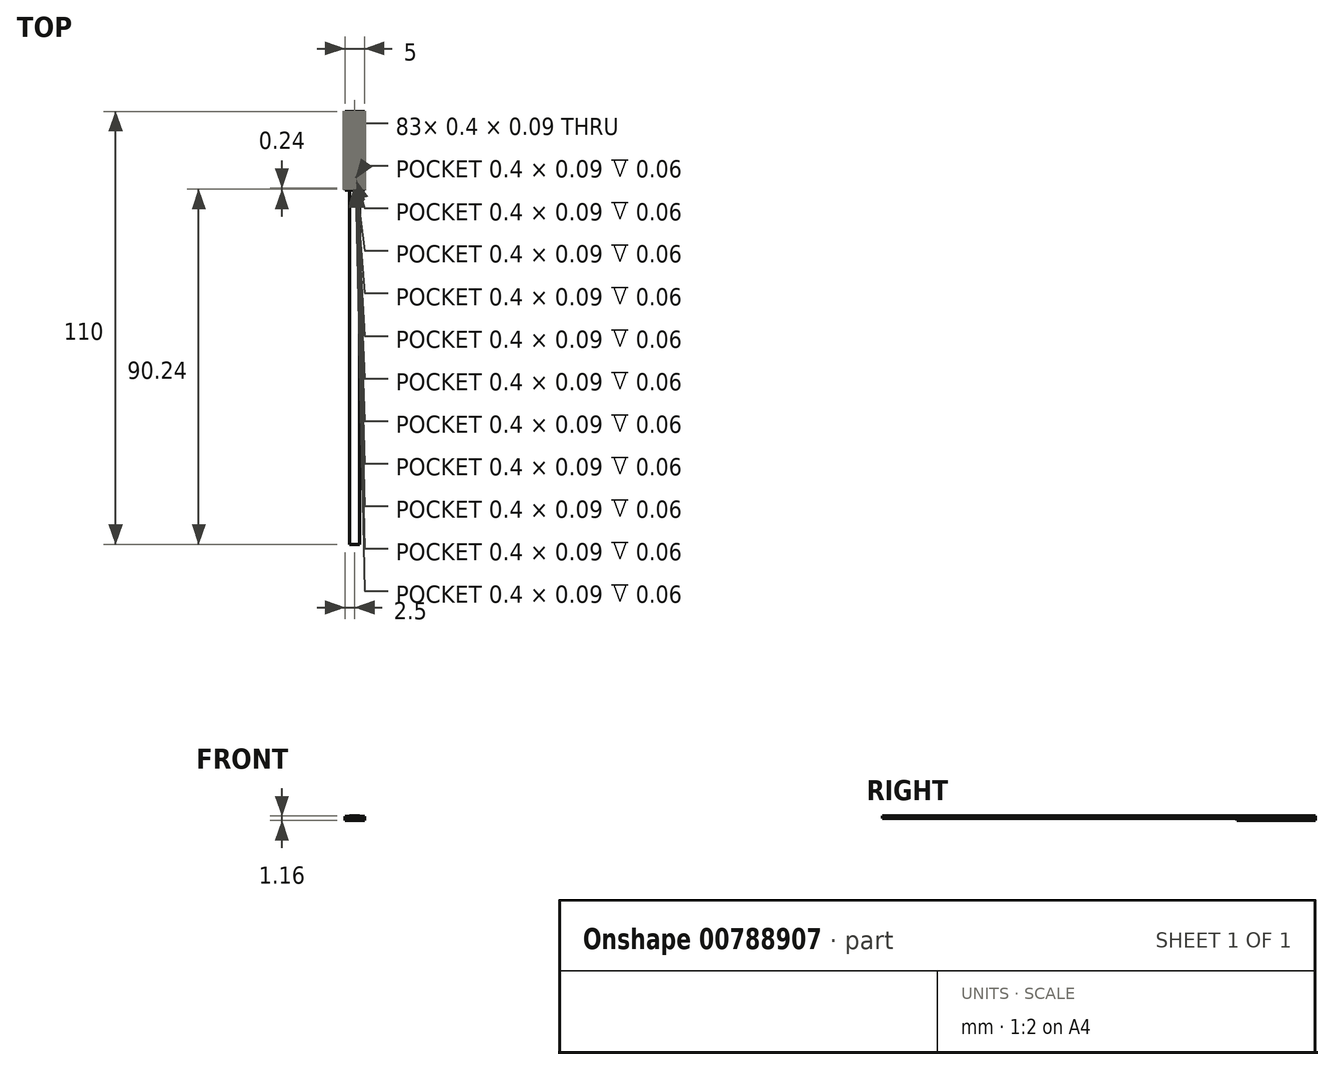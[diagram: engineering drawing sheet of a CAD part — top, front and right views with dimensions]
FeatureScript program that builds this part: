
annotation { "Feature Type Name" : "Feature", "Feature Type Description" : "" }
export const myFeature = defineFeature(function(context is Context, id is Id, definition is map)
    precondition{}
    {
        {
            assignVariable(context, id + "F0", {"name" : "Lz", "anyValue" : 20 * mm});
        }
        {
            var Q0;
            Q0=qCreatedBy(makeId("Top.planeOp"),FACE);
            var sketch = newSketch(context, id + "F1", { "sketchPlane" : qUnion([Q0])});
            skLineSegment(sketch, "E0.bottom", {"start": v(1.25, 10) * mm, "end": v(-1.25, 10) * mm});
            skLineSegment(sketch, "E0.top", {"start": v(1.25, -10) * mm, "end": v(-1.25, -10) * mm});
            skLineSegment(sketch, "E0.left", {"start": v(1.25, 10) * mm, "end": v(1.25, -10) * mm});
            skLineSegment(sketch, "E0.right", {"start": v(-1.25, 10) * mm, "end": v(-1.25, -10) * mm});
            skPoint(sketch, "E0.middle", {"position": v(0, 0) * mm});
            skLineSegment(sketch, "E1.bottom", {"start": v(2.5, 10) * mm, "end": v(-2.5, 10) * mm});
            skLineSegment(sketch, "E1.top", {"start": v(2.5, -10) * mm, "end": v(-2.5, -10) * mm});
            skLineSegment(sketch, "E1.left", {"start": v(2.5, 10) * mm, "end": v(2.5, -10) * mm});
            skLineSegment(sketch, "E1.right", {"start": v(-2.5, 10) * mm, "end": v(-2.5, -10) * mm});
            skSolve(sketch);
        }
        {
            var Q0;
            Q0=qCreatedBy(makeId("Front.planeOp"),FACE);
            var sketch = newSketch(context, id + "F2", { "sketchPlane" : qUnion([Q0])});
            skPoint(sketch, "E2", {"position": v(0.06, -0.1) * mm});
            skEllipse(sketch, "E3", {"center": v(0, -0.17) * mm, "majorRadius": 1.28 * mm, "minorRadius": 0.29 * mm, "majorAxis": v(-1, 0)});
            skSolve(sketch);
        }
        {
            var Q0;
            Q0=makeQuery(id+"F2.imprint","IMPRINT",FACE,{"disambiguationData":[TD([[makeQuery(id+"F2.imprint","IMPRINT",EDGE,{"derivedFrom":sQuery(id+"F2.wireOp",EDGE,"E3")}),1.0]])]});
            extrude(context, id + "F3", {"entities" : qUnion([Q0]), "depth" : 100 * mm, "offsetDistance" : 25 * mm, "hasSecondDirection" : true, "secondDirectionOppositeDirection" : false, "secondDirectionDepth" : getVariable(context, 'Lz') / 2});
        }
        {
            assignVariable(context, id + "F4", {"name" : "tox", "anyValue" : 0.1});
        }
        {
            assignVariable(context, id + "F5", {"name" : "detch", "anyValue" : 0.06});
        }
        {
            assignVariable(context, id + "F6", {"name" : "Hsi", "anyValue" : 0.5});
        }
        {
            var Q0;
            {var subQ0=sQuery(id+"F1.wireOp",EDGE,"E0.right");Q0=makeQuery(id+"F1.imprint","IMPRINT",FACE,{"disambiguationData":[TD([[makeQuery(id+"F1.imprint","IMPRINT",EDGE,{"derivedFrom":subQ0}),-1.0]])]});}
            var Q1;
            {var subQ0=sQuery(id+"F1.wireOp",EDGE,"E0.left");Q1=makeQuery(id+"F1.imprint","IMPRINT",FACE,{"disambiguationData":[TD([[makeQuery(id+"F1.imprint","IMPRINT",EDGE,{"derivedFrom":subQ0}),-1.0]])]});}
            var Q2;
            {var subQ0=sQuery(id+"F1.wireOp",EDGE,"E0.left");Q2=makeQuery(id+"F1.imprint","IMPRINT",FACE,{"disambiguationData":[TD([[makeQuery(id+"F1.imprint","IMPRINT",EDGE,{"derivedFrom":subQ0}),1.0]])]});}
            extrude(context, id + "F7", {"entities" : qUnion([Q0, Q1, Q2]), "oppositeDirection" : true, "depth" : (getVariable(context, 'Hsi') - getVariable(context, 'detch')) * mm});
        }
        {
            var Q0;
            Q0=makeQuery(id+"F7.opExtrude","CAP_FACE",FACE,{"disambiguationData":[OSD([sQuery(id+"F1.wireOp",EDGE,"E1.bottom"),sQuery(id+"F1.wireOp",EDGE,"E1.top"),sQuery(id+"F1.wireOp",EDGE,"E1.left"),sQuery(id+"F1.wireOp",EDGE,"E1.right")])],"isStart":true});
            extrude(context, id + "F8", {"entities" : qUnion([Q0]), "oppositeDirection" : true, "depth" : 1 * mm, "hasSecondDirection" : true, "secondDirectionOppositeDirection" : true, "secondDirectionDepth" : (getVariable(context, 'Hsi') - getVariable(context, 'detch')) * mm});
        }
        {
            var Q0;
            Q0=qCreatedBy(makeId("Top.planeOp"),FACE);
            var sketch = newSketch(context, id + "F9", { "sketchPlane" : qUnion([Q0])});
            skLineSegment(sketch, "E4.bottom", {"start": v(-1.25, 10) * mm, "end": v(1.25, 10) * mm});
            skLineSegment(sketch, "E4.top", {"start": v(-1.25, -10) * mm, "end": v(1.25, -10) * mm});
            skLineSegment(sketch, "E4.left", {"start": v(-1.25, 10) * mm, "end": v(-1.25, -10) * mm});
            skLineSegment(sketch, "E4.right", {"start": v(1.25, 10) * mm, "end": v(1.25, -10) * mm});
            skPoint(sketch, "E4.middle", {"position": v(0, 0) * mm});
            skSolve(sketch);
        }
        {
            var Q0;
            Q0=makeQuery(id+"F9.imprint","IMPRINT",FACE,{"disambiguationData":[TD([[makeQuery(id+"F9.imprint","IMPRINT",EDGE,{"derivedFrom":sQuery(id+"F9.wireOp",EDGE,"E4.bottom")}),-1.0]])]});
            extrude(context, id + "F10", {"entities" : qUnion([Q0]), "operationType" : NewBodyOperationType.ADD, "depth" : (getVariable(context, 'detch')) * mm});
        }
        {
            var Q0;
            Q0=makeQuery(id+"F10.opExtrude","CAP_FACE",FACE,{"disambiguationData":[OSD([sQuery(id+"F9.wireOp",EDGE,"E4.bottom"),sQuery(id+"F9.wireOp",EDGE,"E4.top"),sQuery(id+"F9.wireOp",EDGE,"E4.left"),sQuery(id+"F9.wireOp",EDGE,"E4.right")])],"isStart":false});
            extrude(context, id + "F11", {"entities" : qUnion([Q0]), "depth" : (getVariable(context, 'tox')) * mm});
        }
        {
            var Q0;
            Q0=makeQuery(id+"F11.opExtrude","CAP_FACE",FACE,{"disambiguationData":[OSD([sQuery(id+"F9.wireOp",EDGE,"E4.bottom"),sQuery(id+"F9.wireOp",EDGE,"E4.top"),sQuery(id+"F9.wireOp",EDGE,"E4.left"),sQuery(id+"F9.wireOp",EDGE,"E4.right")])],"isStart":false});
            var sketch = newSketch(context, id + "F12", { "sketchPlane" : qUnion([Q0])});
            skLineSegment(sketch, "E5.bottom", {"start": v(0.2, -9.96) * mm, "end": v(-0.2, -9.96) * mm});
            skLineSegment(sketch, "E5.top", {"start": v(0.2, -10.04) * mm, "end": v(-0.2, -10.04) * mm});
            skLineSegment(sketch, "E5.left", {"start": v(0.2, -9.96) * mm, "end": v(0.2, -10.05) * mm});
            skLineSegment(sketch, "E5.right", {"start": v(-0.2, -9.96) * mm, "end": v(-0.2, -10.05) * mm});
            skPoint(sketch, "E5.middle", {"position": v(0, -10) * mm});
            skLineSegment(sketch, "E6.0.1.0", {"start": v(0.2, -9.72) * mm, "end": v(0.2, -9.8) * mm});
            skLineSegment(sketch, "E6.0.1.1", {"start": v(0.2, -9.8) * mm, "end": v(-0.2, -9.8) * mm});
            skLineSegment(sketch, "E6.0.1.2", {"start": v(-0.2, -9.72) * mm, "end": v(-0.2, -9.8) * mm});
            skLineSegment(sketch, "E6.0.1.3", {"start": v(0.2, -9.72) * mm, "end": v(-0.2, -9.72) * mm});
            skPoint(sketch, "E6.0.1.4", {"position": v(0, -9.76) * mm});
            skLineSegment(sketch, "E6.0.2.0", {"start": v(0.2, -9.48) * mm, "end": v(0.2, -9.57) * mm});
            skLineSegment(sketch, "E6.0.2.1", {"start": v(0.2, -9.56) * mm, "end": v(-0.2, -9.56) * mm});
            skLineSegment(sketch, "E6.0.2.2", {"start": v(-0.2, -9.48) * mm, "end": v(-0.2, -9.57) * mm});
            skLineSegment(sketch, "E6.0.2.3", {"start": v(0.2, -9.48) * mm, "end": v(-0.2, -9.48) * mm});
            skPoint(sketch, "E6.0.2.4", {"position": v(0, -9.52) * mm});
            skLineSegment(sketch, "E6.0.3.0", {"start": v(0.2, -9.24) * mm, "end": v(0.2, -9.33) * mm});
            skLineSegment(sketch, "E6.0.3.1", {"start": v(0.2, -9.32) * mm, "end": v(-0.2, -9.32) * mm});
            skLineSegment(sketch, "E6.0.3.2", {"start": v(-0.2, -9.24) * mm, "end": v(-0.2, -9.33) * mm});
            skLineSegment(sketch, "E6.0.3.3", {"start": v(0.2, -9.24) * mm, "end": v(-0.2, -9.24) * mm});
            skPoint(sketch, "E6.0.3.4", {"position": v(0, -9.28) * mm});
            skLineSegment(sketch, "E6.0.4.0", {"start": v(0.2, -9) * mm, "end": v(0.2, -9.09) * mm});
            skLineSegment(sketch, "E6.0.4.1", {"start": v(0.2, -9.08) * mm, "end": v(-0.2, -9.08) * mm});
            skLineSegment(sketch, "E6.0.4.2", {"start": v(-0.2, -9) * mm, "end": v(-0.2, -9.09) * mm});
            skLineSegment(sketch, "E6.0.4.3", {"start": v(0.2, -9) * mm, "end": v(-0.2, -9) * mm});
            skPoint(sketch, "E6.0.4.4", {"position": v(0, -9.04) * mm});
            skLineSegment(sketch, "E6.0.5.0", {"start": v(0.2, -8.76) * mm, "end": v(0.2, -8.85) * mm});
            skLineSegment(sketch, "E6.0.5.1", {"start": v(0.2, -8.84) * mm, "end": v(-0.2, -8.84) * mm});
            skLineSegment(sketch, "E6.0.5.2", {"start": v(-0.2, -8.76) * mm, "end": v(-0.2, -8.85) * mm});
            skLineSegment(sketch, "E6.0.5.3", {"start": v(0.2, -8.76) * mm, "end": v(-0.2, -8.76) * mm});
            skPoint(sketch, "E6.0.5.4", {"position": v(0, -8.8) * mm});
            skLineSegment(sketch, "E6.0.6.0", {"start": v(0.2, -8.52) * mm, "end": v(0.2, -8.6) * mm});
            skLineSegment(sketch, "E6.0.6.1", {"start": v(0.2, -8.6) * mm, "end": v(-0.2, -8.6) * mm});
            skLineSegment(sketch, "E6.0.6.2", {"start": v(-0.2, -8.52) * mm, "end": v(-0.2, -8.6) * mm});
            skLineSegment(sketch, "E6.0.6.3", {"start": v(0.2, -8.52) * mm, "end": v(-0.2, -8.52) * mm});
            skPoint(sketch, "E6.0.6.4", {"position": v(0, -8.56) * mm});
            skLineSegment(sketch, "E6.0.7.0", {"start": v(0.2, -8.28) * mm, "end": v(0.2, -8.37) * mm});
            skLineSegment(sketch, "E6.0.7.1", {"start": v(0.2, -8.36) * mm, "end": v(-0.2, -8.36) * mm});
            skLineSegment(sketch, "E6.0.7.2", {"start": v(-0.2, -8.28) * mm, "end": v(-0.2, -8.37) * mm});
            skLineSegment(sketch, "E6.0.7.3", {"start": v(0.2, -8.28) * mm, "end": v(-0.2, -8.28) * mm});
            skPoint(sketch, "E6.0.7.4", {"position": v(0, -8.32) * mm});
            skLineSegment(sketch, "E6.0.8.0", {"start": v(0.2, -8.04) * mm, "end": v(0.2, -8.13) * mm});
            skLineSegment(sketch, "E6.0.8.1", {"start": v(0.2, -8.12) * mm, "end": v(-0.2, -8.12) * mm});
            skLineSegment(sketch, "E6.0.8.2", {"start": v(-0.2, -8.04) * mm, "end": v(-0.2, -8.13) * mm});
            skLineSegment(sketch, "E6.0.8.3", {"start": v(0.2, -8.04) * mm, "end": v(-0.2, -8.04) * mm});
            skPoint(sketch, "E6.0.8.4", {"position": v(0, -8.08) * mm});
            skLineSegment(sketch, "E6.0.9.0", {"start": v(0.2, -7.8) * mm, "end": v(0.2, -7.89) * mm});
            skLineSegment(sketch, "E6.0.9.1", {"start": v(0.2, -7.88) * mm, "end": v(-0.2, -7.88) * mm});
            skLineSegment(sketch, "E6.0.9.2", {"start": v(-0.2, -7.8) * mm, "end": v(-0.2, -7.89) * mm});
            skLineSegment(sketch, "E6.0.9.3", {"start": v(0.2, -7.8) * mm, "end": v(-0.2, -7.8) * mm});
            skPoint(sketch, "E6.0.9.4", {"position": v(0, -7.84) * mm});
            skLineSegment(sketch, "E6.direction1", {"start": v(-0.2, -10.04) * mm, "end": v(24.8, -10.04) * mm, "construction": true});
            skLineSegment(sketch, "E6.direction2", {"start": v(-0.2, -10.05) * mm, "end": v(-0.2, -9.8) * mm, "construction": true});
            skLineSegment(sketch, "E7.0.0.10", {"start": v(0.2, -7.56) * mm, "end": v(0.2, -7.65) * mm});
            skLineSegment(sketch, "E7.3.0.10", {"start": v(0.2, -7.64) * mm, "end": v(-0.2, -7.64) * mm});
            skLineSegment(sketch, "E7.6.0.10", {"start": v(-0.2, -7.56) * mm, "end": v(-0.2, -7.65) * mm});
            skLineSegment(sketch, "E7.9.0.10", {"start": v(0.2, -7.56) * mm, "end": v(-0.2, -7.56) * mm});
            skPoint(sketch, "E7.12.0.10", {"position": v(0, -7.6) * mm});
            skLineSegment(sketch, "E7.0.0.11", {"start": v(0.2, -7.32) * mm, "end": v(0.2, -7.4) * mm});
            skLineSegment(sketch, "E7.3.0.11", {"start": v(0.2, -7.4) * mm, "end": v(-0.2, -7.4) * mm});
            skLineSegment(sketch, "E7.6.0.11", {"start": v(-0.2, -7.32) * mm, "end": v(-0.2, -7.4) * mm});
            skLineSegment(sketch, "E7.9.0.11", {"start": v(0.2, -7.32) * mm, "end": v(-0.2, -7.32) * mm});
            skPoint(sketch, "E7.12.0.11", {"position": v(0, -7.36) * mm});
            skLineSegment(sketch, "E7.0.0.12", {"start": v(0.2, -7.08) * mm, "end": v(0.2, -7.17) * mm});
            skLineSegment(sketch, "E7.3.0.12", {"start": v(0.2, -7.16) * mm, "end": v(-0.2, -7.16) * mm});
            skLineSegment(sketch, "E7.6.0.12", {"start": v(-0.2, -7.08) * mm, "end": v(-0.2, -7.17) * mm});
            skLineSegment(sketch, "E7.9.0.12", {"start": v(0.2, -7.08) * mm, "end": v(-0.2, -7.08) * mm});
            skPoint(sketch, "E7.12.0.12", {"position": v(0, -7.12) * mm});
            skLineSegment(sketch, "E7.0.0.13", {"start": v(0.2, -6.84) * mm, "end": v(0.2, -6.93) * mm});
            skLineSegment(sketch, "E7.3.0.13", {"start": v(0.2, -6.92) * mm, "end": v(-0.2, -6.92) * mm});
            skLineSegment(sketch, "E7.6.0.13", {"start": v(-0.2, -6.84) * mm, "end": v(-0.2, -6.93) * mm});
            skLineSegment(sketch, "E7.9.0.13", {"start": v(0.2, -6.84) * mm, "end": v(-0.2, -6.84) * mm});
            skPoint(sketch, "E7.12.0.13", {"position": v(0, -6.88) * mm});
            skLineSegment(sketch, "E7.0.0.14", {"start": v(0.2, -6.6) * mm, "end": v(0.2, -6.69) * mm});
            skLineSegment(sketch, "E7.3.0.14", {"start": v(0.2, -6.68) * mm, "end": v(-0.2, -6.68) * mm});
            skLineSegment(sketch, "E7.6.0.14", {"start": v(-0.2, -6.6) * mm, "end": v(-0.2, -6.69) * mm});
            skLineSegment(sketch, "E7.9.0.14", {"start": v(0.2, -6.6) * mm, "end": v(-0.2, -6.6) * mm});
            skPoint(sketch, "E7.12.0.14", {"position": v(0, -6.64) * mm});
            skLineSegment(sketch, "E7.0.0.15", {"start": v(0.2, -6.36) * mm, "end": v(0.2, -6.45) * mm});
            skLineSegment(sketch, "E7.3.0.15", {"start": v(0.2, -6.44) * mm, "end": v(-0.2, -6.44) * mm});
            skLineSegment(sketch, "E7.6.0.15", {"start": v(-0.2, -6.36) * mm, "end": v(-0.2, -6.45) * mm});
            skLineSegment(sketch, "E7.9.0.15", {"start": v(0.2, -6.36) * mm, "end": v(-0.2, -6.36) * mm});
            skPoint(sketch, "E7.12.0.15", {"position": v(0, -6.4) * mm});
            skLineSegment(sketch, "E7.0.0.16", {"start": v(0.2, -6.12) * mm, "end": v(0.2, -6.2) * mm});
            skLineSegment(sketch, "E7.3.0.16", {"start": v(0.2, -6.2) * mm, "end": v(-0.2, -6.2) * mm});
            skLineSegment(sketch, "E7.6.0.16", {"start": v(-0.2, -6.12) * mm, "end": v(-0.2, -6.2) * mm});
            skLineSegment(sketch, "E7.9.0.16", {"start": v(0.2, -6.12) * mm, "end": v(-0.2, -6.12) * mm});
            skPoint(sketch, "E7.12.0.16", {"position": v(0, -6.16) * mm});
            skLineSegment(sketch, "E7.0.0.17", {"start": v(0.2, -5.88) * mm, "end": v(0.2, -5.97) * mm});
            skLineSegment(sketch, "E7.3.0.17", {"start": v(0.2, -5.96) * mm, "end": v(-0.2, -5.96) * mm});
            skLineSegment(sketch, "E7.6.0.17", {"start": v(-0.2, -5.88) * mm, "end": v(-0.2, -5.97) * mm});
            skLineSegment(sketch, "E7.9.0.17", {"start": v(0.2, -5.88) * mm, "end": v(-0.2, -5.88) * mm});
            skPoint(sketch, "E7.12.0.17", {"position": v(0, -5.92) * mm});
            skLineSegment(sketch, "E7.0.0.18", {"start": v(0.2, -5.64) * mm, "end": v(0.2, -5.73) * mm});
            skLineSegment(sketch, "E7.3.0.18", {"start": v(0.2, -5.72) * mm, "end": v(-0.2, -5.72) * mm});
            skLineSegment(sketch, "E7.6.0.18", {"start": v(-0.2, -5.64) * mm, "end": v(-0.2, -5.73) * mm});
            skLineSegment(sketch, "E7.9.0.18", {"start": v(0.2, -5.64) * mm, "end": v(-0.2, -5.64) * mm});
            skPoint(sketch, "E7.12.0.18", {"position": v(0, -5.68) * mm});
            skLineSegment(sketch, "E7.0.0.19", {"start": v(0.2, -5.4) * mm, "end": v(0.2, -5.49) * mm});
            skLineSegment(sketch, "E7.3.0.19", {"start": v(0.2, -5.48) * mm, "end": v(-0.2, -5.48) * mm});
            skLineSegment(sketch, "E7.6.0.19", {"start": v(-0.2, -5.4) * mm, "end": v(-0.2, -5.49) * mm});
            skLineSegment(sketch, "E7.9.0.19", {"start": v(0.2, -5.4) * mm, "end": v(-0.2, -5.4) * mm});
            skPoint(sketch, "E7.12.0.19", {"position": v(0, -5.44) * mm});
            skLineSegment(sketch, "E7.0.0.20", {"start": v(0.2, -5.16) * mm, "end": v(0.2, -5.25) * mm});
            skLineSegment(sketch, "E7.3.0.20", {"start": v(0.2, -5.24) * mm, "end": v(-0.2, -5.24) * mm});
            skLineSegment(sketch, "E7.6.0.20", {"start": v(-0.2, -5.16) * mm, "end": v(-0.2, -5.25) * mm});
            skLineSegment(sketch, "E7.9.0.20", {"start": v(0.2, -5.16) * mm, "end": v(-0.2, -5.16) * mm});
            skPoint(sketch, "E7.12.0.20", {"position": v(0, -5.2) * mm});
            skLineSegment(sketch, "E7.0.0.21", {"start": v(0.2, -4.92) * mm, "end": v(0.2, -5) * mm});
            skLineSegment(sketch, "E7.3.0.21", {"start": v(0.2, -5) * mm, "end": v(-0.2, -5) * mm});
            skLineSegment(sketch, "E7.6.0.21", {"start": v(-0.2, -4.92) * mm, "end": v(-0.2, -5) * mm});
            skLineSegment(sketch, "E7.9.0.21", {"start": v(0.2, -4.92) * mm, "end": v(-0.2, -4.92) * mm});
            skPoint(sketch, "E7.12.0.21", {"position": v(0, -4.96) * mm});
            skLineSegment(sketch, "E7.0.0.22", {"start": v(0.2, -4.68) * mm, "end": v(0.2, -4.77) * mm});
            skLineSegment(sketch, "E7.3.0.22", {"start": v(0.2, -4.76) * mm, "end": v(-0.2, -4.76) * mm});
            skLineSegment(sketch, "E7.6.0.22", {"start": v(-0.2, -4.68) * mm, "end": v(-0.2, -4.77) * mm});
            skLineSegment(sketch, "E7.9.0.22", {"start": v(0.2, -4.68) * mm, "end": v(-0.2, -4.68) * mm});
            skPoint(sketch, "E7.12.0.22", {"position": v(0, -4.72) * mm});
            skLineSegment(sketch, "E7.0.0.23", {"start": v(0.2, -4.44) * mm, "end": v(0.2, -4.53) * mm});
            skLineSegment(sketch, "E7.3.0.23", {"start": v(0.2, -4.52) * mm, "end": v(-0.2, -4.52) * mm});
            skLineSegment(sketch, "E7.6.0.23", {"start": v(-0.2, -4.44) * mm, "end": v(-0.2, -4.53) * mm});
            skLineSegment(sketch, "E7.9.0.23", {"start": v(0.2, -4.44) * mm, "end": v(-0.2, -4.44) * mm});
            skPoint(sketch, "E7.12.0.23", {"position": v(0, -4.48) * mm});
            skLineSegment(sketch, "E7.0.0.24", {"start": v(0.2, -4.2) * mm, "end": v(0.2, -4.29) * mm});
            skLineSegment(sketch, "E7.3.0.24", {"start": v(0.2, -4.28) * mm, "end": v(-0.2, -4.28) * mm});
            skLineSegment(sketch, "E7.6.0.24", {"start": v(-0.2, -4.2) * mm, "end": v(-0.2, -4.29) * mm});
            skLineSegment(sketch, "E7.9.0.24", {"start": v(0.2, -4.2) * mm, "end": v(-0.2, -4.2) * mm});
            skPoint(sketch, "E7.12.0.24", {"position": v(0, -4.24) * mm});
            skLineSegment(sketch, "E7.0.0.25", {"start": v(0.2, -3.96) * mm, "end": v(0.2, -4.05) * mm});
            skLineSegment(sketch, "E7.3.0.25", {"start": v(0.2, -4.04) * mm, "end": v(-0.2, -4.04) * mm});
            skLineSegment(sketch, "E7.6.0.25", {"start": v(-0.2, -3.96) * mm, "end": v(-0.2, -4.05) * mm});
            skLineSegment(sketch, "E7.9.0.25", {"start": v(0.2, -3.96) * mm, "end": v(-0.2, -3.96) * mm});
            skPoint(sketch, "E7.12.0.25", {"position": v(0, -4) * mm});
            skLineSegment(sketch, "E7.0.0.26", {"start": v(0.2, -3.72) * mm, "end": v(0.2, -3.8) * mm});
            skLineSegment(sketch, "E7.3.0.26", {"start": v(0.2, -3.8) * mm, "end": v(-0.2, -3.8) * mm});
            skLineSegment(sketch, "E7.6.0.26", {"start": v(-0.2, -3.72) * mm, "end": v(-0.2, -3.8) * mm});
            skLineSegment(sketch, "E7.9.0.26", {"start": v(0.2, -3.72) * mm, "end": v(-0.2, -3.72) * mm});
            skPoint(sketch, "E7.12.0.26", {"position": v(0, -3.76) * mm});
            skLineSegment(sketch, "E7.0.0.27", {"start": v(0.2, -3.48) * mm, "end": v(0.2, -3.57) * mm});
            skLineSegment(sketch, "E7.3.0.27", {"start": v(0.2, -3.56) * mm, "end": v(-0.2, -3.56) * mm});
            skLineSegment(sketch, "E7.6.0.27", {"start": v(-0.2, -3.48) * mm, "end": v(-0.2, -3.57) * mm});
            skLineSegment(sketch, "E7.9.0.27", {"start": v(0.2, -3.48) * mm, "end": v(-0.2, -3.48) * mm});
            skPoint(sketch, "E7.12.0.27", {"position": v(0, -3.52) * mm});
            skLineSegment(sketch, "E7.0.0.28", {"start": v(0.2, -3.24) * mm, "end": v(0.2, -3.33) * mm});
            skLineSegment(sketch, "E7.3.0.28", {"start": v(0.2, -3.32) * mm, "end": v(-0.2, -3.32) * mm});
            skLineSegment(sketch, "E7.6.0.28", {"start": v(-0.2, -3.24) * mm, "end": v(-0.2, -3.33) * mm});
            skLineSegment(sketch, "E7.9.0.28", {"start": v(0.2, -3.24) * mm, "end": v(-0.2, -3.24) * mm});
            skPoint(sketch, "E7.12.0.28", {"position": v(0, -3.28) * mm});
            skLineSegment(sketch, "E7.0.0.29", {"start": v(0.2, -3) * mm, "end": v(0.2, -3.09) * mm});
            skLineSegment(sketch, "E7.3.0.29", {"start": v(0.2, -3.08) * mm, "end": v(-0.2, -3.08) * mm});
            skLineSegment(sketch, "E7.6.0.29", {"start": v(-0.2, -3) * mm, "end": v(-0.2, -3.09) * mm});
            skLineSegment(sketch, "E7.9.0.29", {"start": v(0.2, -3) * mm, "end": v(-0.2, -3) * mm});
            skPoint(sketch, "E7.12.0.29", {"position": v(0, -3.04) * mm});
            skLineSegment(sketch, "E7.0.0.30", {"start": v(0.2, -2.76) * mm, "end": v(0.2, -2.85) * mm});
            skLineSegment(sketch, "E7.3.0.30", {"start": v(0.2, -2.84) * mm, "end": v(-0.2, -2.84) * mm});
            skLineSegment(sketch, "E7.6.0.30", {"start": v(-0.2, -2.76) * mm, "end": v(-0.2, -2.85) * mm});
            skLineSegment(sketch, "E7.9.0.30", {"start": v(0.2, -2.76) * mm, "end": v(-0.2, -2.76) * mm});
            skPoint(sketch, "E7.12.0.30", {"position": v(0, -2.8) * mm});
            skLineSegment(sketch, "E7.0.0.31", {"start": v(0.2, -2.52) * mm, "end": v(0.2, -2.6) * mm});
            skLineSegment(sketch, "E7.3.0.31", {"start": v(0.2, -2.6) * mm, "end": v(-0.2, -2.6) * mm});
            skLineSegment(sketch, "E7.6.0.31", {"start": v(-0.2, -2.52) * mm, "end": v(-0.2, -2.6) * mm});
            skLineSegment(sketch, "E7.9.0.31", {"start": v(0.2, -2.52) * mm, "end": v(-0.2, -2.52) * mm});
            skPoint(sketch, "E7.12.0.31", {"position": v(0, -2.56) * mm});
            skLineSegment(sketch, "E7.0.0.32", {"start": v(0.2, -2.28) * mm, "end": v(0.2, -2.37) * mm});
            skLineSegment(sketch, "E7.3.0.32", {"start": v(0.2, -2.36) * mm, "end": v(-0.2, -2.36) * mm});
            skLineSegment(sketch, "E7.6.0.32", {"start": v(-0.2, -2.28) * mm, "end": v(-0.2, -2.37) * mm});
            skLineSegment(sketch, "E7.9.0.32", {"start": v(0.2, -2.28) * mm, "end": v(-0.2, -2.28) * mm});
            skPoint(sketch, "E7.12.0.32", {"position": v(0, -2.32) * mm});
            skLineSegment(sketch, "E7.0.0.33", {"start": v(0.2, -2.04) * mm, "end": v(0.2, -2.13) * mm});
            skLineSegment(sketch, "E7.3.0.33", {"start": v(0.2, -2.12) * mm, "end": v(-0.2, -2.12) * mm});
            skLineSegment(sketch, "E7.6.0.33", {"start": v(-0.2, -2.04) * mm, "end": v(-0.2, -2.13) * mm});
            skLineSegment(sketch, "E7.9.0.33", {"start": v(0.2, -2.04) * mm, "end": v(-0.2, -2.04) * mm});
            skPoint(sketch, "E7.12.0.33", {"position": v(0, -2.08) * mm});
            skLineSegment(sketch, "E7.0.0.34", {"start": v(0.2, -1.8) * mm, "end": v(0.2, -1.89) * mm});
            skLineSegment(sketch, "E7.3.0.34", {"start": v(0.2, -1.88) * mm, "end": v(-0.2, -1.88) * mm});
            skLineSegment(sketch, "E7.6.0.34", {"start": v(-0.2, -1.8) * mm, "end": v(-0.2, -1.89) * mm});
            skLineSegment(sketch, "E7.9.0.34", {"start": v(0.2, -1.8) * mm, "end": v(-0.2, -1.8) * mm});
            skPoint(sketch, "E7.12.0.34", {"position": v(0, -1.84) * mm});
            skLineSegment(sketch, "E7.0.0.35", {"start": v(0.2, -1.56) * mm, "end": v(0.2, -1.65) * mm});
            skLineSegment(sketch, "E7.3.0.35", {"start": v(0.2, -1.64) * mm, "end": v(-0.2, -1.64) * mm});
            skLineSegment(sketch, "E7.6.0.35", {"start": v(-0.2, -1.56) * mm, "end": v(-0.2, -1.65) * mm});
            skLineSegment(sketch, "E7.9.0.35", {"start": v(0.2, -1.56) * mm, "end": v(-0.2, -1.56) * mm});
            skPoint(sketch, "E7.12.0.35", {"position": v(0, -1.6) * mm});
            skLineSegment(sketch, "E7.0.0.36", {"start": v(0.2, -1.32) * mm, "end": v(0.2, -1.4) * mm});
            skLineSegment(sketch, "E7.3.0.36", {"start": v(0.2, -1.4) * mm, "end": v(-0.2, -1.4) * mm});
            skLineSegment(sketch, "E7.6.0.36", {"start": v(-0.2, -1.32) * mm, "end": v(-0.2, -1.4) * mm});
            skLineSegment(sketch, "E7.9.0.36", {"start": v(0.2, -1.32) * mm, "end": v(-0.2, -1.32) * mm});
            skPoint(sketch, "E7.12.0.36", {"position": v(0, -1.36) * mm});
            skLineSegment(sketch, "E7.0.0.37", {"start": v(0.2, -1.08) * mm, "end": v(0.2, -1.17) * mm});
            skLineSegment(sketch, "E7.3.0.37", {"start": v(0.2, -1.16) * mm, "end": v(-0.2, -1.16) * mm});
            skLineSegment(sketch, "E7.6.0.37", {"start": v(-0.2, -1.08) * mm, "end": v(-0.2, -1.17) * mm});
            skLineSegment(sketch, "E7.9.0.37", {"start": v(0.2, -1.08) * mm, "end": v(-0.2, -1.08) * mm});
            skPoint(sketch, "E7.12.0.37", {"position": v(0, -1.12) * mm});
            skLineSegment(sketch, "E7.0.0.38", {"start": v(0.2, -0.84) * mm, "end": v(0.2, -0.93) * mm});
            skLineSegment(sketch, "E7.3.0.38", {"start": v(0.2, -0.92) * mm, "end": v(-0.2, -0.92) * mm});
            skLineSegment(sketch, "E7.6.0.38", {"start": v(-0.2, -0.84) * mm, "end": v(-0.2, -0.93) * mm});
            skLineSegment(sketch, "E7.9.0.38", {"start": v(0.2, -0.84) * mm, "end": v(-0.2, -0.84) * mm});
            skPoint(sketch, "E7.12.0.38", {"position": v(0, -0.88) * mm});
            skLineSegment(sketch, "E7.0.0.39", {"start": v(0.2, -0.6) * mm, "end": v(0.2, -0.69) * mm});
            skLineSegment(sketch, "E7.3.0.39", {"start": v(0.2, -0.68) * mm, "end": v(-0.2, -0.68) * mm});
            skLineSegment(sketch, "E7.6.0.39", {"start": v(-0.2, -0.6) * mm, "end": v(-0.2, -0.69) * mm});
            skLineSegment(sketch, "E7.9.0.39", {"start": v(0.2, -0.6) * mm, "end": v(-0.2, -0.6) * mm});
            skPoint(sketch, "E7.12.0.39", {"position": v(0, -0.64) * mm});
            skLineSegment(sketch, "E7.0.0.40", {"start": v(0.2, -0.36) * mm, "end": v(0.2, -0.45) * mm});
            skLineSegment(sketch, "E7.3.0.40", {"start": v(0.2, -0.44) * mm, "end": v(-0.2, -0.44) * mm});
            skLineSegment(sketch, "E7.6.0.40", {"start": v(-0.2, -0.36) * mm, "end": v(-0.2, -0.45) * mm});
            skLineSegment(sketch, "E7.9.0.40", {"start": v(0.2, -0.36) * mm, "end": v(-0.2, -0.36) * mm});
            skPoint(sketch, "E7.12.0.40", {"position": v(0, -0.4) * mm});
            skLineSegment(sketch, "E7.0.0.41", {"start": v(0.2, -0.12) * mm, "end": v(0.2, -0.2) * mm});
            skLineSegment(sketch, "E7.3.0.41", {"start": v(0.2, -0.2) * mm, "end": v(-0.2, -0.2) * mm});
            skLineSegment(sketch, "E7.6.0.41", {"start": v(-0.2, -0.12) * mm, "end": v(-0.2, -0.2) * mm});
            skLineSegment(sketch, "E7.9.0.41", {"start": v(0.2, -0.12) * mm, "end": v(-0.2, -0.12) * mm});
            skPoint(sketch, "E7.12.0.41", {"position": v(0, -0.16) * mm});
            skLineSegment(sketch, "E8.0.0.42", {"start": v(0.2, 0.12) * mm, "end": v(0.2, 0.03) * mm});
            skLineSegment(sketch, "E8.3.0.42", {"start": v(0.2, 0.04) * mm, "end": v(-0.2, 0.04) * mm});
            skLineSegment(sketch, "E8.6.0.42", {"start": v(-0.2, 0.12) * mm, "end": v(-0.2, 0.03) * mm});
            skLineSegment(sketch, "E8.9.0.42", {"start": v(0.2, 0.12) * mm, "end": v(-0.2, 0.12) * mm});
            skPoint(sketch, "E8.12.0.42", {"position": v(0, 0.08) * mm});
            skLineSegment(sketch, "E8.0.0.43", {"start": v(0.2, 0.36) * mm, "end": v(0.2, 0.27) * mm});
            skLineSegment(sketch, "E8.3.0.43", {"start": v(0.2, 0.28) * mm, "end": v(-0.2, 0.28) * mm});
            skLineSegment(sketch, "E8.6.0.43", {"start": v(-0.2, 0.36) * mm, "end": v(-0.2, 0.27) * mm});
            skLineSegment(sketch, "E8.9.0.43", {"start": v(0.2, 0.36) * mm, "end": v(-0.2, 0.36) * mm});
            skPoint(sketch, "E8.12.0.43", {"position": v(0, 0.32) * mm});
            skLineSegment(sketch, "E8.0.0.44", {"start": v(0.2, 0.6) * mm, "end": v(0.2, 0.51) * mm});
            skLineSegment(sketch, "E8.3.0.44", {"start": v(0.2, 0.52) * mm, "end": v(-0.2, 0.52) * mm});
            skLineSegment(sketch, "E8.6.0.44", {"start": v(-0.2, 0.6) * mm, "end": v(-0.2, 0.51) * mm});
            skLineSegment(sketch, "E8.9.0.44", {"start": v(0.2, 0.6) * mm, "end": v(-0.2, 0.6) * mm});
            skPoint(sketch, "E8.12.0.44", {"position": v(0, 0.56) * mm});
            skLineSegment(sketch, "E8.0.0.45", {"start": v(0.2, 0.84) * mm, "end": v(0.2, 0.75) * mm});
            skLineSegment(sketch, "E8.3.0.45", {"start": v(0.2, 0.76) * mm, "end": v(-0.2, 0.76) * mm});
            skLineSegment(sketch, "E8.6.0.45", {"start": v(-0.2, 0.84) * mm, "end": v(-0.2, 0.75) * mm});
            skLineSegment(sketch, "E8.9.0.45", {"start": v(0.2, 0.84) * mm, "end": v(-0.2, 0.84) * mm});
            skPoint(sketch, "E8.12.0.45", {"position": v(0, 0.8) * mm});
            skLineSegment(sketch, "E8.0.0.46", {"start": v(0.2, 1.08) * mm, "end": v(0.2, 1) * mm});
            skLineSegment(sketch, "E8.3.0.46", {"start": v(0.2, 1) * mm, "end": v(-0.2, 1) * mm});
            skLineSegment(sketch, "E8.6.0.46", {"start": v(-0.2, 1.08) * mm, "end": v(-0.2, 1) * mm});
            skLineSegment(sketch, "E8.9.0.46", {"start": v(0.2, 1.08) * mm, "end": v(-0.2, 1.08) * mm});
            skPoint(sketch, "E8.12.0.46", {"position": v(0, 1.04) * mm});
            skLineSegment(sketch, "E8.0.0.47", {"start": v(0.2, 1.32) * mm, "end": v(0.2, 1.23) * mm});
            skLineSegment(sketch, "E8.3.0.47", {"start": v(0.2, 1.23) * mm, "end": v(-0.2, 1.23) * mm});
            skLineSegment(sketch, "E8.6.0.47", {"start": v(-0.2, 1.32) * mm, "end": v(-0.2, 1.23) * mm});
            skLineSegment(sketch, "E8.9.0.47", {"start": v(0.2, 1.32) * mm, "end": v(-0.2, 1.32) * mm});
            skPoint(sketch, "E8.12.0.47", {"position": v(0, 1.28) * mm});
            skLineSegment(sketch, "E8.0.0.48", {"start": v(0.2, 1.56) * mm, "end": v(0.2, 1.47) * mm});
            skLineSegment(sketch, "E8.3.0.48", {"start": v(0.2, 1.48) * mm, "end": v(-0.2, 1.48) * mm});
            skLineSegment(sketch, "E8.6.0.48", {"start": v(-0.2, 1.56) * mm, "end": v(-0.2, 1.47) * mm});
            skLineSegment(sketch, "E8.9.0.48", {"start": v(0.2, 1.56) * mm, "end": v(-0.2, 1.56) * mm});
            skPoint(sketch, "E8.12.0.48", {"position": v(0, 1.52) * mm});
            skLineSegment(sketch, "E8.0.0.49", {"start": v(0.2, 1.8) * mm, "end": v(0.2, 1.71) * mm});
            skLineSegment(sketch, "E8.3.0.49", {"start": v(0.2, 1.72) * mm, "end": v(-0.2, 1.72) * mm});
            skLineSegment(sketch, "E8.6.0.49", {"start": v(-0.2, 1.8) * mm, "end": v(-0.2, 1.71) * mm});
            skLineSegment(sketch, "E8.9.0.49", {"start": v(0.2, 1.8) * mm, "end": v(-0.2, 1.8) * mm});
            skPoint(sketch, "E8.12.0.49", {"position": v(0, 1.76) * mm});
            skLineSegment(sketch, "E8.0.0.50", {"start": v(0.2, 2.04) * mm, "end": v(0.2, 1.95) * mm});
            skLineSegment(sketch, "E8.3.0.50", {"start": v(0.2, 1.96) * mm, "end": v(-0.2, 1.96) * mm});
            skLineSegment(sketch, "E8.6.0.50", {"start": v(-0.2, 2.04) * mm, "end": v(-0.2, 1.95) * mm});
            skLineSegment(sketch, "E8.9.0.50", {"start": v(0.2, 2.04) * mm, "end": v(-0.2, 2.04) * mm});
            skPoint(sketch, "E8.12.0.50", {"position": v(0, 2) * mm});
            skLineSegment(sketch, "E8.0.0.51", {"start": v(0.2, 2.28) * mm, "end": v(0.2, 2.2) * mm});
            skLineSegment(sketch, "E8.3.0.51", {"start": v(0.2, 2.2) * mm, "end": v(-0.2, 2.2) * mm});
            skLineSegment(sketch, "E8.6.0.51", {"start": v(-0.2, 2.28) * mm, "end": v(-0.2, 2.2) * mm});
            skLineSegment(sketch, "E8.9.0.51", {"start": v(0.2, 2.28) * mm, "end": v(-0.2, 2.28) * mm});
            skPoint(sketch, "E8.12.0.51", {"position": v(0, 2.24) * mm});
            skLineSegment(sketch, "E8.0.0.52", {"start": v(0.2, 2.52) * mm, "end": v(0.2, 2.43) * mm});
            skLineSegment(sketch, "E8.3.0.52", {"start": v(0.2, 2.44) * mm, "end": v(-0.2, 2.44) * mm});
            skLineSegment(sketch, "E8.6.0.52", {"start": v(-0.2, 2.52) * mm, "end": v(-0.2, 2.43) * mm});
            skLineSegment(sketch, "E8.9.0.52", {"start": v(0.2, 2.52) * mm, "end": v(-0.2, 2.52) * mm});
            skPoint(sketch, "E8.12.0.52", {"position": v(0, 2.48) * mm});
            skLineSegment(sketch, "E8.0.0.53", {"start": v(0.2, 2.76) * mm, "end": v(0.2, 2.67) * mm});
            skLineSegment(sketch, "E8.3.0.53", {"start": v(0.2, 2.68) * mm, "end": v(-0.2, 2.68) * mm});
            skLineSegment(sketch, "E8.6.0.53", {"start": v(-0.2, 2.76) * mm, "end": v(-0.2, 2.67) * mm});
            skLineSegment(sketch, "E8.9.0.53", {"start": v(0.2, 2.76) * mm, "end": v(-0.2, 2.76) * mm});
            skPoint(sketch, "E8.12.0.53", {"position": v(0, 2.72) * mm});
            skLineSegment(sketch, "E8.0.0.54", {"start": v(0.2, 3) * mm, "end": v(0.2, 2.91) * mm});
            skLineSegment(sketch, "E8.3.0.54", {"start": v(0.2, 2.92) * mm, "end": v(-0.2, 2.92) * mm});
            skLineSegment(sketch, "E8.6.0.54", {"start": v(-0.2, 3) * mm, "end": v(-0.2, 2.91) * mm});
            skLineSegment(sketch, "E8.9.0.54", {"start": v(0.2, 3) * mm, "end": v(-0.2, 3) * mm});
            skPoint(sketch, "E8.12.0.54", {"position": v(0, 2.96) * mm});
            skLineSegment(sketch, "E8.0.0.55", {"start": v(0.2, 3.24) * mm, "end": v(0.2, 3.15) * mm});
            skLineSegment(sketch, "E8.3.0.55", {"start": v(0.2, 3.16) * mm, "end": v(-0.2, 3.16) * mm});
            skLineSegment(sketch, "E8.6.0.55", {"start": v(-0.2, 3.24) * mm, "end": v(-0.2, 3.15) * mm});
            skLineSegment(sketch, "E8.9.0.55", {"start": v(0.2, 3.24) * mm, "end": v(-0.2, 3.24) * mm});
            skPoint(sketch, "E8.12.0.55", {"position": v(0, 3.2) * mm});
            skLineSegment(sketch, "E8.0.0.56", {"start": v(0.2, 3.48) * mm, "end": v(0.2, 3.4) * mm});
            skLineSegment(sketch, "E8.3.0.56", {"start": v(0.2, 3.4) * mm, "end": v(-0.2, 3.4) * mm});
            skLineSegment(sketch, "E8.6.0.56", {"start": v(-0.2, 3.48) * mm, "end": v(-0.2, 3.4) * mm});
            skLineSegment(sketch, "E8.9.0.56", {"start": v(0.2, 3.48) * mm, "end": v(-0.2, 3.48) * mm});
            skPoint(sketch, "E8.12.0.56", {"position": v(0, 3.44) * mm});
            skLineSegment(sketch, "E8.0.0.57", {"start": v(0.2, 3.72) * mm, "end": v(0.2, 3.63) * mm});
            skLineSegment(sketch, "E8.3.0.57", {"start": v(0.2, 3.63) * mm, "end": v(-0.2, 3.63) * mm});
            skLineSegment(sketch, "E8.6.0.57", {"start": v(-0.2, 3.72) * mm, "end": v(-0.2, 3.63) * mm});
            skLineSegment(sketch, "E8.9.0.57", {"start": v(0.2, 3.72) * mm, "end": v(-0.2, 3.72) * mm});
            skPoint(sketch, "E8.12.0.57", {"position": v(0, 3.68) * mm});
            skLineSegment(sketch, "E8.0.0.58", {"start": v(0.2, 3.96) * mm, "end": v(0.2, 3.87) * mm});
            skLineSegment(sketch, "E8.3.0.58", {"start": v(0.2, 3.88) * mm, "end": v(-0.2, 3.88) * mm});
            skLineSegment(sketch, "E8.6.0.58", {"start": v(-0.2, 3.96) * mm, "end": v(-0.2, 3.87) * mm});
            skLineSegment(sketch, "E8.9.0.58", {"start": v(0.2, 3.96) * mm, "end": v(-0.2, 3.96) * mm});
            skPoint(sketch, "E8.12.0.58", {"position": v(0, 3.92) * mm});
            skLineSegment(sketch, "E8.0.0.59", {"start": v(0.2, 4.2) * mm, "end": v(0.2, 4.11) * mm});
            skLineSegment(sketch, "E8.3.0.59", {"start": v(0.2, 4.12) * mm, "end": v(-0.2, 4.12) * mm});
            skLineSegment(sketch, "E8.6.0.59", {"start": v(-0.2, 4.2) * mm, "end": v(-0.2, 4.11) * mm});
            skLineSegment(sketch, "E8.9.0.59", {"start": v(0.2, 4.2) * mm, "end": v(-0.2, 4.2) * mm});
            skPoint(sketch, "E8.12.0.59", {"position": v(0, 4.16) * mm});
            skLineSegment(sketch, "E8.0.0.60", {"start": v(0.2, 4.44) * mm, "end": v(0.2, 4.35) * mm});
            skLineSegment(sketch, "E8.3.0.60", {"start": v(0.2, 4.35) * mm, "end": v(-0.2, 4.35) * mm});
            skLineSegment(sketch, "E8.6.0.60", {"start": v(-0.2, 4.44) * mm, "end": v(-0.2, 4.35) * mm});
            skLineSegment(sketch, "E8.9.0.60", {"start": v(0.2, 4.44) * mm, "end": v(-0.2, 4.44) * mm});
            skPoint(sketch, "E8.12.0.60", {"position": v(0, 4.4) * mm});
            skLineSegment(sketch, "E8.0.0.61", {"start": v(0.2, 4.68) * mm, "end": v(0.2, 4.6) * mm});
            skLineSegment(sketch, "E8.3.0.61", {"start": v(0.2, 4.6) * mm, "end": v(-0.2, 4.6) * mm});
            skLineSegment(sketch, "E8.6.0.61", {"start": v(-0.2, 4.68) * mm, "end": v(-0.2, 4.6) * mm});
            skLineSegment(sketch, "E8.9.0.61", {"start": v(0.2, 4.68) * mm, "end": v(-0.2, 4.68) * mm});
            skPoint(sketch, "E8.12.0.61", {"position": v(0, 4.64) * mm});
            skLineSegment(sketch, "E8.0.0.62", {"start": v(0.2, 4.92) * mm, "end": v(0.2, 4.83) * mm});
            skLineSegment(sketch, "E8.3.0.62", {"start": v(0.2, 4.83) * mm, "end": v(-0.2, 4.83) * mm});
            skLineSegment(sketch, "E8.6.0.62", {"start": v(-0.2, 4.92) * mm, "end": v(-0.2, 4.83) * mm});
            skLineSegment(sketch, "E8.9.0.62", {"start": v(0.2, 4.92) * mm, "end": v(-0.2, 4.92) * mm});
            skPoint(sketch, "E8.12.0.62", {"position": v(0, 4.88) * mm});
            skLineSegment(sketch, "E8.0.0.63", {"start": v(0.2, 5.16) * mm, "end": v(0.2, 5.07) * mm});
            skLineSegment(sketch, "E8.3.0.63", {"start": v(0.2, 5.07) * mm, "end": v(-0.2, 5.07) * mm});
            skLineSegment(sketch, "E8.6.0.63", {"start": v(-0.2, 5.16) * mm, "end": v(-0.2, 5.07) * mm});
            skLineSegment(sketch, "E8.9.0.63", {"start": v(0.2, 5.16) * mm, "end": v(-0.2, 5.16) * mm});
            skPoint(sketch, "E8.12.0.63", {"position": v(0, 5.12) * mm});
            skLineSegment(sketch, "E8.0.0.64", {"start": v(0.2, 5.4) * mm, "end": v(0.2, 5.31) * mm});
            skLineSegment(sketch, "E8.3.0.64", {"start": v(0.2, 5.32) * mm, "end": v(-0.2, 5.32) * mm});
            skLineSegment(sketch, "E8.6.0.64", {"start": v(-0.2, 5.4) * mm, "end": v(-0.2, 5.31) * mm});
            skLineSegment(sketch, "E8.9.0.64", {"start": v(0.2, 5.4) * mm, "end": v(-0.2, 5.4) * mm});
            skPoint(sketch, "E8.12.0.64", {"position": v(0, 5.36) * mm});
            skLineSegment(sketch, "E8.0.0.65", {"start": v(0.2, 5.64) * mm, "end": v(0.2, 5.55) * mm});
            skLineSegment(sketch, "E8.3.0.65", {"start": v(0.2, 5.56) * mm, "end": v(-0.2, 5.56) * mm});
            skLineSegment(sketch, "E8.6.0.65", {"start": v(-0.2, 5.64) * mm, "end": v(-0.2, 5.55) * mm});
            skLineSegment(sketch, "E8.9.0.65", {"start": v(0.2, 5.64) * mm, "end": v(-0.2, 5.64) * mm});
            skPoint(sketch, "E8.12.0.65", {"position": v(0, 5.6) * mm});
            skLineSegment(sketch, "E8.0.0.66", {"start": v(0.2, 5.88) * mm, "end": v(0.2, 5.8) * mm});
            skLineSegment(sketch, "E8.3.0.66", {"start": v(0.2, 5.8) * mm, "end": v(-0.2, 5.8) * mm});
            skLineSegment(sketch, "E8.6.0.66", {"start": v(-0.2, 5.88) * mm, "end": v(-0.2, 5.8) * mm});
            skLineSegment(sketch, "E8.9.0.66", {"start": v(0.2, 5.88) * mm, "end": v(-0.2, 5.88) * mm});
            skPoint(sketch, "E8.12.0.66", {"position": v(0, 5.84) * mm});
            skLineSegment(sketch, "E8.0.0.67", {"start": v(0.2, 6.12) * mm, "end": v(0.2, 6.03) * mm});
            skLineSegment(sketch, "E8.3.0.67", {"start": v(0.2, 6.03) * mm, "end": v(-0.2, 6.03) * mm});
            skLineSegment(sketch, "E8.6.0.67", {"start": v(-0.2, 6.12) * mm, "end": v(-0.2, 6.03) * mm});
            skLineSegment(sketch, "E8.9.0.67", {"start": v(0.2, 6.12) * mm, "end": v(-0.2, 6.12) * mm});
            skPoint(sketch, "E8.12.0.67", {"position": v(0, 6.08) * mm});
            skLineSegment(sketch, "E8.0.0.68", {"start": v(0.2, 6.36) * mm, "end": v(0.2, 6.27) * mm});
            skLineSegment(sketch, "E8.3.0.68", {"start": v(0.2, 6.28) * mm, "end": v(-0.2, 6.28) * mm});
            skLineSegment(sketch, "E8.6.0.68", {"start": v(-0.2, 6.36) * mm, "end": v(-0.2, 6.27) * mm});
            skLineSegment(sketch, "E8.9.0.68", {"start": v(0.2, 6.36) * mm, "end": v(-0.2, 6.36) * mm});
            skPoint(sketch, "E8.12.0.68", {"position": v(0, 6.32) * mm});
            skLineSegment(sketch, "E8.0.0.69", {"start": v(0.2, 6.6) * mm, "end": v(0.2, 6.51) * mm});
            skLineSegment(sketch, "E8.3.0.69", {"start": v(0.2, 6.51) * mm, "end": v(-0.2, 6.51) * mm});
            skLineSegment(sketch, "E8.6.0.69", {"start": v(-0.2, 6.6) * mm, "end": v(-0.2, 6.51) * mm});
            skLineSegment(sketch, "E8.9.0.69", {"start": v(0.2, 6.6) * mm, "end": v(-0.2, 6.6) * mm});
            skPoint(sketch, "E8.12.0.69", {"position": v(0, 6.56) * mm});
            skLineSegment(sketch, "E8.0.0.70", {"start": v(0.2, 6.84) * mm, "end": v(0.2, 6.75) * mm});
            skLineSegment(sketch, "E8.3.0.70", {"start": v(0.2, 6.75) * mm, "end": v(-0.2, 6.75) * mm});
            skLineSegment(sketch, "E8.6.0.70", {"start": v(-0.2, 6.84) * mm, "end": v(-0.2, 6.75) * mm});
            skLineSegment(sketch, "E8.9.0.70", {"start": v(0.2, 6.84) * mm, "end": v(-0.2, 6.84) * mm});
            skPoint(sketch, "E8.12.0.70", {"position": v(0, 6.8) * mm});
            skLineSegment(sketch, "E8.0.0.71", {"start": v(0.2, 7.08) * mm, "end": v(0.2, 7) * mm});
            skLineSegment(sketch, "E8.3.0.71", {"start": v(0.2, 7) * mm, "end": v(-0.2, 7) * mm});
            skLineSegment(sketch, "E8.6.0.71", {"start": v(-0.2, 7.08) * mm, "end": v(-0.2, 7) * mm});
            skLineSegment(sketch, "E8.9.0.71", {"start": v(0.2, 7.08) * mm, "end": v(-0.2, 7.08) * mm});
            skPoint(sketch, "E8.12.0.71", {"position": v(0, 7.04) * mm});
            skLineSegment(sketch, "E8.0.0.72", {"start": v(0.2, 7.32) * mm, "end": v(0.2, 7.23) * mm});
            skLineSegment(sketch, "E8.3.0.72", {"start": v(0.2, 7.23) * mm, "end": v(-0.2, 7.23) * mm});
            skLineSegment(sketch, "E8.6.0.72", {"start": v(-0.2, 7.32) * mm, "end": v(-0.2, 7.23) * mm});
            skLineSegment(sketch, "E8.9.0.72", {"start": v(0.2, 7.32) * mm, "end": v(-0.2, 7.32) * mm});
            skPoint(sketch, "E8.12.0.72", {"position": v(0, 7.28) * mm});
            skLineSegment(sketch, "E8.0.0.73", {"start": v(0.2, 7.56) * mm, "end": v(0.2, 7.47) * mm});
            skLineSegment(sketch, "E8.3.0.73", {"start": v(0.2, 7.47) * mm, "end": v(-0.2, 7.47) * mm});
            skLineSegment(sketch, "E8.6.0.73", {"start": v(-0.2, 7.56) * mm, "end": v(-0.2, 7.47) * mm});
            skLineSegment(sketch, "E8.9.0.73", {"start": v(0.2, 7.56) * mm, "end": v(-0.2, 7.56) * mm});
            skPoint(sketch, "E8.12.0.73", {"position": v(0, 7.52) * mm});
            skLineSegment(sketch, "E8.0.0.74", {"start": v(0.2, 7.8) * mm, "end": v(0.2, 7.71) * mm});
            skLineSegment(sketch, "E8.3.0.74", {"start": v(0.2, 7.71) * mm, "end": v(-0.2, 7.71) * mm});
            skLineSegment(sketch, "E8.6.0.74", {"start": v(-0.2, 7.8) * mm, "end": v(-0.2, 7.71) * mm});
            skLineSegment(sketch, "E8.9.0.74", {"start": v(0.2, 7.8) * mm, "end": v(-0.2, 7.8) * mm});
            skPoint(sketch, "E8.12.0.74", {"position": v(0, 7.76) * mm});
            skLineSegment(sketch, "E8.0.0.75", {"start": v(0.2, 8.04) * mm, "end": v(0.2, 7.95) * mm});
            skLineSegment(sketch, "E8.3.0.75", {"start": v(0.2, 7.95) * mm, "end": v(-0.2, 7.95) * mm});
            skLineSegment(sketch, "E8.6.0.75", {"start": v(-0.2, 8.04) * mm, "end": v(-0.2, 7.95) * mm});
            skLineSegment(sketch, "E8.9.0.75", {"start": v(0.2, 8.04) * mm, "end": v(-0.2, 8.04) * mm});
            skPoint(sketch, "E8.12.0.75", {"position": v(0, 8) * mm});
            skLineSegment(sketch, "E8.0.0.76", {"start": v(0.2, 8.28) * mm, "end": v(0.2, 8.2) * mm});
            skLineSegment(sketch, "E8.3.0.76", {"start": v(0.2, 8.2) * mm, "end": v(-0.2, 8.2) * mm});
            skLineSegment(sketch, "E8.6.0.76", {"start": v(-0.2, 8.28) * mm, "end": v(-0.2, 8.2) * mm});
            skLineSegment(sketch, "E8.9.0.76", {"start": v(0.2, 8.28) * mm, "end": v(-0.2, 8.28) * mm});
            skPoint(sketch, "E8.12.0.76", {"position": v(0, 8.24) * mm});
            skLineSegment(sketch, "E8.0.0.77", {"start": v(0.2, 8.52) * mm, "end": v(0.2, 8.43) * mm});
            skLineSegment(sketch, "E8.3.0.77", {"start": v(0.2, 8.43) * mm, "end": v(-0.2, 8.43) * mm});
            skLineSegment(sketch, "E8.6.0.77", {"start": v(-0.2, 8.52) * mm, "end": v(-0.2, 8.43) * mm});
            skLineSegment(sketch, "E8.9.0.77", {"start": v(0.2, 8.52) * mm, "end": v(-0.2, 8.52) * mm});
            skPoint(sketch, "E8.12.0.77", {"position": v(0, 8.48) * mm});
            skLineSegment(sketch, "E8.0.0.78", {"start": v(0.2, 8.76) * mm, "end": v(0.2, 8.67) * mm});
            skLineSegment(sketch, "E8.3.0.78", {"start": v(0.2, 8.67) * mm, "end": v(-0.2, 8.67) * mm});
            skLineSegment(sketch, "E8.6.0.78", {"start": v(-0.2, 8.76) * mm, "end": v(-0.2, 8.67) * mm});
            skLineSegment(sketch, "E8.9.0.78", {"start": v(0.2, 8.76) * mm, "end": v(-0.2, 8.76) * mm});
            skPoint(sketch, "E8.12.0.78", {"position": v(0, 8.72) * mm});
            skLineSegment(sketch, "E8.0.0.79", {"start": v(0.2, 9) * mm, "end": v(0.2, 8.91) * mm});
            skLineSegment(sketch, "E8.3.0.79", {"start": v(0.2, 8.91) * mm, "end": v(-0.2, 8.91) * mm});
            skLineSegment(sketch, "E8.6.0.79", {"start": v(-0.2, 9) * mm, "end": v(-0.2, 8.91) * mm});
            skLineSegment(sketch, "E8.9.0.79", {"start": v(0.2, 9) * mm, "end": v(-0.2, 9) * mm});
            skPoint(sketch, "E8.12.0.79", {"position": v(0, 8.96) * mm});
            skLineSegment(sketch, "E8.0.0.80", {"start": v(0.2, 9.24) * mm, "end": v(0.2, 9.15) * mm});
            skLineSegment(sketch, "E8.3.0.80", {"start": v(0.2, 9.15) * mm, "end": v(-0.2, 9.15) * mm});
            skLineSegment(sketch, "E8.6.0.80", {"start": v(-0.2, 9.24) * mm, "end": v(-0.2, 9.15) * mm});
            skLineSegment(sketch, "E8.9.0.80", {"start": v(0.2, 9.24) * mm, "end": v(-0.2, 9.24) * mm});
            skPoint(sketch, "E8.12.0.80", {"position": v(0, 9.2) * mm});
            skLineSegment(sketch, "E8.0.0.81", {"start": v(0.2, 9.48) * mm, "end": v(0.2, 9.4) * mm});
            skLineSegment(sketch, "E8.3.0.81", {"start": v(0.2, 9.4) * mm, "end": v(-0.2, 9.4) * mm});
            skLineSegment(sketch, "E8.6.0.81", {"start": v(-0.2, 9.48) * mm, "end": v(-0.2, 9.4) * mm});
            skLineSegment(sketch, "E8.9.0.81", {"start": v(0.2, 9.48) * mm, "end": v(-0.2, 9.48) * mm});
            skPoint(sketch, "E8.12.0.81", {"position": v(0, 9.44) * mm});
            skLineSegment(sketch, "E8.0.0.82", {"start": v(0.2, 9.72) * mm, "end": v(0.2, 9.63) * mm});
            skLineSegment(sketch, "E8.3.0.82", {"start": v(0.2, 9.63) * mm, "end": v(-0.2, 9.63) * mm});
            skLineSegment(sketch, "E8.6.0.82", {"start": v(-0.2, 9.72) * mm, "end": v(-0.2, 9.63) * mm});
            skLineSegment(sketch, "E8.9.0.82", {"start": v(0.2, 9.72) * mm, "end": v(-0.2, 9.72) * mm});
            skPoint(sketch, "E8.12.0.82", {"position": v(0, 9.68) * mm});
            skLineSegment(sketch, "E8.0.0.83", {"start": v(0.2, 9.96) * mm, "end": v(0.2, 9.87) * mm});
            skLineSegment(sketch, "E8.3.0.83", {"start": v(0.2, 9.87) * mm, "end": v(-0.2, 9.87) * mm});
            skLineSegment(sketch, "E8.6.0.83", {"start": v(-0.2, 9.96) * mm, "end": v(-0.2, 9.87) * mm});
            skLineSegment(sketch, "E8.9.0.83", {"start": v(0.2, 9.96) * mm, "end": v(-0.2, 9.96) * mm});
            skPoint(sketch, "E8.12.0.83", {"position": v(0, 9.92) * mm});
            skLineSegment(sketch, "E8.0.0.84", {"start": v(0.2, 10.2) * mm, "end": v(0.2, 10.11) * mm});
            skLineSegment(sketch, "E8.3.0.84", {"start": v(0.2, 10.11) * mm, "end": v(-0.2, 10.11) * mm});
            skLineSegment(sketch, "E8.6.0.84", {"start": v(-0.2, 10.2) * mm, "end": v(-0.2, 10.11) * mm});
            skLineSegment(sketch, "E8.9.0.84", {"start": v(0.2, 10.2) * mm, "end": v(-0.2, 10.2) * mm});
            skPoint(sketch, "E8.12.0.84", {"position": v(0, 10.16) * mm});
            skLineSegment(sketch, "E8.0.0.85", {"start": v(0.2, 10.44) * mm, "end": v(0.2, 10.35) * mm});
            skLineSegment(sketch, "E8.3.0.85", {"start": v(0.2, 10.35) * mm, "end": v(-0.2, 10.35) * mm});
            skLineSegment(sketch, "E8.6.0.85", {"start": v(-0.2, 10.44) * mm, "end": v(-0.2, 10.35) * mm});
            skLineSegment(sketch, "E8.9.0.85", {"start": v(0.2, 10.44) * mm, "end": v(-0.2, 10.44) * mm});
            skPoint(sketch, "E8.12.0.85", {"position": v(0, 10.4) * mm});
            skLineSegment(sketch, "E8.0.0.86", {"start": v(0.2, 10.68) * mm, "end": v(0.2, 10.6) * mm});
            skLineSegment(sketch, "E8.3.0.86", {"start": v(0.2, 10.6) * mm, "end": v(-0.2, 10.6) * mm});
            skLineSegment(sketch, "E8.6.0.86", {"start": v(-0.2, 10.68) * mm, "end": v(-0.2, 10.6) * mm});
            skLineSegment(sketch, "E8.9.0.86", {"start": v(0.2, 10.68) * mm, "end": v(-0.2, 10.68) * mm});
            skPoint(sketch, "E8.12.0.86", {"position": v(0, 10.64) * mm});
            skLineSegment(sketch, "E8.0.0.87", {"start": v(0.2, 10.92) * mm, "end": v(0.2, 10.83) * mm});
            skLineSegment(sketch, "E8.3.0.87", {"start": v(0.2, 10.83) * mm, "end": v(-0.2, 10.83) * mm});
            skLineSegment(sketch, "E8.6.0.87", {"start": v(-0.2, 10.92) * mm, "end": v(-0.2, 10.83) * mm});
            skLineSegment(sketch, "E8.9.0.87", {"start": v(0.2, 10.92) * mm, "end": v(-0.2, 10.92) * mm});
            skPoint(sketch, "E8.12.0.87", {"position": v(0, 10.88) * mm});
            skLineSegment(sketch, "E8.0.0.88", {"start": v(0.2, 11.16) * mm, "end": v(0.2, 11.07) * mm});
            skLineSegment(sketch, "E8.3.0.88", {"start": v(0.2, 11.07) * mm, "end": v(-0.2, 11.07) * mm});
            skLineSegment(sketch, "E8.6.0.88", {"start": v(-0.2, 11.16) * mm, "end": v(-0.2, 11.07) * mm});
            skLineSegment(sketch, "E8.9.0.88", {"start": v(0.2, 11.16) * mm, "end": v(-0.2, 11.16) * mm});
            skPoint(sketch, "E8.12.0.88", {"position": v(0, 11.12) * mm});
            skLineSegment(sketch, "E8.0.0.89", {"start": v(0.2, 11.4) * mm, "end": v(0.2, 11.31) * mm});
            skLineSegment(sketch, "E8.3.0.89", {"start": v(0.2, 11.31) * mm, "end": v(-0.2, 11.31) * mm});
            skLineSegment(sketch, "E8.6.0.89", {"start": v(-0.2, 11.4) * mm, "end": v(-0.2, 11.31) * mm});
            skLineSegment(sketch, "E8.9.0.89", {"start": v(0.2, 11.4) * mm, "end": v(-0.2, 11.4) * mm});
            skPoint(sketch, "E8.12.0.89", {"position": v(0, 11.36) * mm});
            skLineSegment(sketch, "E8.0.0.90", {"start": v(0.2, 11.64) * mm, "end": v(0.2, 11.55) * mm});
            skLineSegment(sketch, "E8.3.0.90", {"start": v(0.2, 11.55) * mm, "end": v(-0.2, 11.55) * mm});
            skLineSegment(sketch, "E8.6.0.90", {"start": v(-0.2, 11.64) * mm, "end": v(-0.2, 11.55) * mm});
            skLineSegment(sketch, "E8.9.0.90", {"start": v(0.2, 11.64) * mm, "end": v(-0.2, 11.64) * mm});
            skPoint(sketch, "E8.12.0.90", {"position": v(0, 11.6) * mm});
            skLineSegment(sketch, "E8.0.0.91", {"start": v(0.2, 11.88) * mm, "end": v(0.2, 11.8) * mm});
            skLineSegment(sketch, "E8.3.0.91", {"start": v(0.2, 11.8) * mm, "end": v(-0.2, 11.8) * mm});
            skLineSegment(sketch, "E8.6.0.91", {"start": v(-0.2, 11.88) * mm, "end": v(-0.2, 11.8) * mm});
            skLineSegment(sketch, "E8.9.0.91", {"start": v(0.2, 11.88) * mm, "end": v(-0.2, 11.88) * mm});
            skPoint(sketch, "E8.12.0.91", {"position": v(0, 11.84) * mm});
            skLineSegment(sketch, "E8.0.0.92", {"start": v(0.2, 12.12) * mm, "end": v(0.2, 12.03) * mm});
            skLineSegment(sketch, "E8.3.0.92", {"start": v(0.2, 12.03) * mm, "end": v(-0.2, 12.03) * mm});
            skLineSegment(sketch, "E8.6.0.92", {"start": v(-0.2, 12.12) * mm, "end": v(-0.2, 12.03) * mm});
            skLineSegment(sketch, "E8.9.0.92", {"start": v(0.2, 12.12) * mm, "end": v(-0.2, 12.12) * mm});
            skPoint(sketch, "E8.12.0.92", {"position": v(0, 12.08) * mm});
            skLineSegment(sketch, "E8.0.0.93", {"start": v(0.2, 12.36) * mm, "end": v(0.2, 12.27) * mm});
            skLineSegment(sketch, "E8.3.0.93", {"start": v(0.2, 12.27) * mm, "end": v(-0.2, 12.27) * mm});
            skLineSegment(sketch, "E8.6.0.93", {"start": v(-0.2, 12.36) * mm, "end": v(-0.2, 12.27) * mm});
            skLineSegment(sketch, "E8.9.0.93", {"start": v(0.2, 12.36) * mm, "end": v(-0.2, 12.36) * mm});
            skPoint(sketch, "E8.12.0.93", {"position": v(0, 12.32) * mm});
            skLineSegment(sketch, "E8.0.0.94", {"start": v(0.2, 12.6) * mm, "end": v(0.2, 12.51) * mm});
            skLineSegment(sketch, "E8.3.0.94", {"start": v(0.2, 12.51) * mm, "end": v(-0.2, 12.51) * mm});
            skLineSegment(sketch, "E8.6.0.94", {"start": v(-0.2, 12.6) * mm, "end": v(-0.2, 12.51) * mm});
            skLineSegment(sketch, "E8.9.0.94", {"start": v(0.2, 12.6) * mm, "end": v(-0.2, 12.6) * mm});
            skPoint(sketch, "E8.12.0.94", {"position": v(0, 12.56) * mm});
            skLineSegment(sketch, "E8.0.0.95", {"start": v(0.2, 12.84) * mm, "end": v(0.2, 12.75) * mm});
            skLineSegment(sketch, "E8.3.0.95", {"start": v(0.2, 12.75) * mm, "end": v(-0.2, 12.75) * mm});
            skLineSegment(sketch, "E8.6.0.95", {"start": v(-0.2, 12.84) * mm, "end": v(-0.2, 12.75) * mm});
            skLineSegment(sketch, "E8.9.0.95", {"start": v(0.2, 12.84) * mm, "end": v(-0.2, 12.84) * mm});
            skPoint(sketch, "E8.12.0.95", {"position": v(0, 12.8) * mm});
            skLineSegment(sketch, "E8.0.0.96", {"start": v(0.2, 13.08) * mm, "end": v(0.2, 13) * mm});
            skLineSegment(sketch, "E8.3.0.96", {"start": v(0.2, 13) * mm, "end": v(-0.2, 13) * mm});
            skLineSegment(sketch, "E8.6.0.96", {"start": v(-0.2, 13.08) * mm, "end": v(-0.2, 13) * mm});
            skLineSegment(sketch, "E8.9.0.96", {"start": v(0.2, 13.08) * mm, "end": v(-0.2, 13.08) * mm});
            skPoint(sketch, "E8.12.0.96", {"position": v(0, 13.04) * mm});
            skLineSegment(sketch, "E8.0.0.97", {"start": v(0.2, 13.32) * mm, "end": v(0.2, 13.23) * mm});
            skLineSegment(sketch, "E8.3.0.97", {"start": v(0.2, 13.23) * mm, "end": v(-0.2, 13.23) * mm});
            skLineSegment(sketch, "E8.6.0.97", {"start": v(-0.2, 13.32) * mm, "end": v(-0.2, 13.23) * mm});
            skLineSegment(sketch, "E8.9.0.97", {"start": v(0.2, 13.32) * mm, "end": v(-0.2, 13.32) * mm});
            skPoint(sketch, "E8.12.0.97", {"position": v(0, 13.28) * mm});
            skLineSegment(sketch, "E8.0.0.98", {"start": v(0.2, 13.56) * mm, "end": v(0.2, 13.47) * mm});
            skLineSegment(sketch, "E8.3.0.98", {"start": v(0.2, 13.47) * mm, "end": v(-0.2, 13.47) * mm});
            skLineSegment(sketch, "E8.6.0.98", {"start": v(-0.2, 13.56) * mm, "end": v(-0.2, 13.47) * mm});
            skLineSegment(sketch, "E8.9.0.98", {"start": v(0.2, 13.56) * mm, "end": v(-0.2, 13.56) * mm});
            skPoint(sketch, "E8.12.0.98", {"position": v(0, 13.52) * mm});
            skLineSegment(sketch, "E8.0.0.99", {"start": v(0.2, 13.8) * mm, "end": v(0.2, 13.71) * mm});
            skLineSegment(sketch, "E8.3.0.99", {"start": v(0.2, 13.71) * mm, "end": v(-0.2, 13.71) * mm});
            skLineSegment(sketch, "E8.6.0.99", {"start": v(-0.2, 13.8) * mm, "end": v(-0.2, 13.71) * mm});
            skLineSegment(sketch, "E8.9.0.99", {"start": v(0.2, 13.8) * mm, "end": v(-0.2, 13.8) * mm});
            skPoint(sketch, "E8.12.0.99", {"position": v(0, 13.76) * mm});
            skSolve(sketch);
        }
        {
            var Q0;
            Q0=qSketchRegion(id+"F12",true);
            extrude(context, id + "F13", {"entities" : qUnion([Q0]), "operationType" : NewBodyOperationType.REMOVE, "oppositeDirection" : true, "depth" : (getVariable(context, 'detch') + getVariable(context, 'tox')) * mm});
        }
        {
            var Q0;
            Q0=qSketchRegion(id+"F2",true);
            extrude(context, id + "F14", {"entities" : qUnion([Q0]), "depth" : getVariable(context, 'Lz') / 2, "offsetDistance" : 25 * mm, "hasSecondDirection" : true, "secondDirectionOppositeDirection" : true, "secondDirectionDepth" : getVariable(context, 'Lz') / 2});
        }
    });
